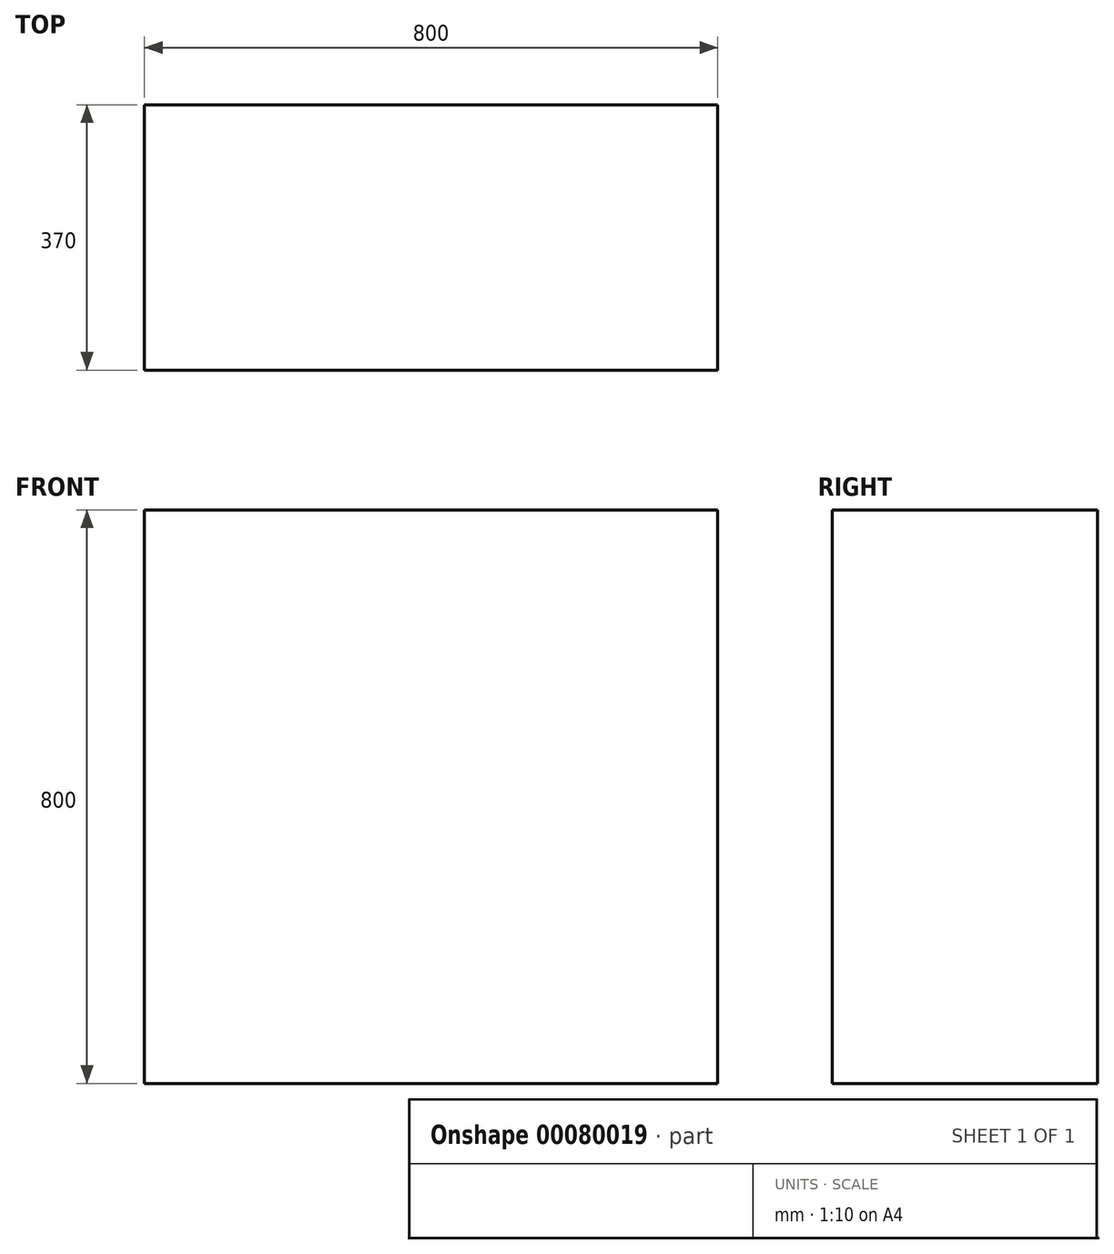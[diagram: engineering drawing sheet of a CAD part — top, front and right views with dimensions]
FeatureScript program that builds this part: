
annotation { "Feature Type Name" : "Feature", "Feature Type Description" : "" }
export const myFeature = defineFeature(function(context is Context, id is Id, definition is map)
    precondition{}
    {
        {
            var Q0;
            Q0=qCreatedBy(makeId("Top.planeOp"),FACE);
            var sketch = newSketch(context, id + "F0", { "sketchPlane" : qUnion([Q0])});
            skLineSegment(sketch, "E0.bottom", {"start": v(0, 0) * mm, "end": v(800, 0) * mm});
            skLineSegment(sketch, "E0.top", {"start": v(0, -370) * mm, "end": v(800, -370) * mm});
            skLineSegment(sketch, "E0.left", {"start": v(0, 0) * mm, "end": v(0, -370) * mm});
            skLineSegment(sketch, "E0.right", {"start": v(800, 0) * mm, "end": v(800, -370) * mm});
            skSolve(sketch);
        }
        {
            var Q0;
            Q0=makeQuery(id+"F0.imprint","IMPRINT",FACE,{"disambiguationData":[TD([[makeQuery(id+"F0.imprint","IMPRINT",EDGE,{"derivedFrom":sQuery(id+"F0.wireOp",EDGE,"E0.bottom")}),-1.0]])]});
            extrude(context, id + "F1", {"entities" : qUnion([Q0]), "depth" : 800 * mm});
        }
    });
